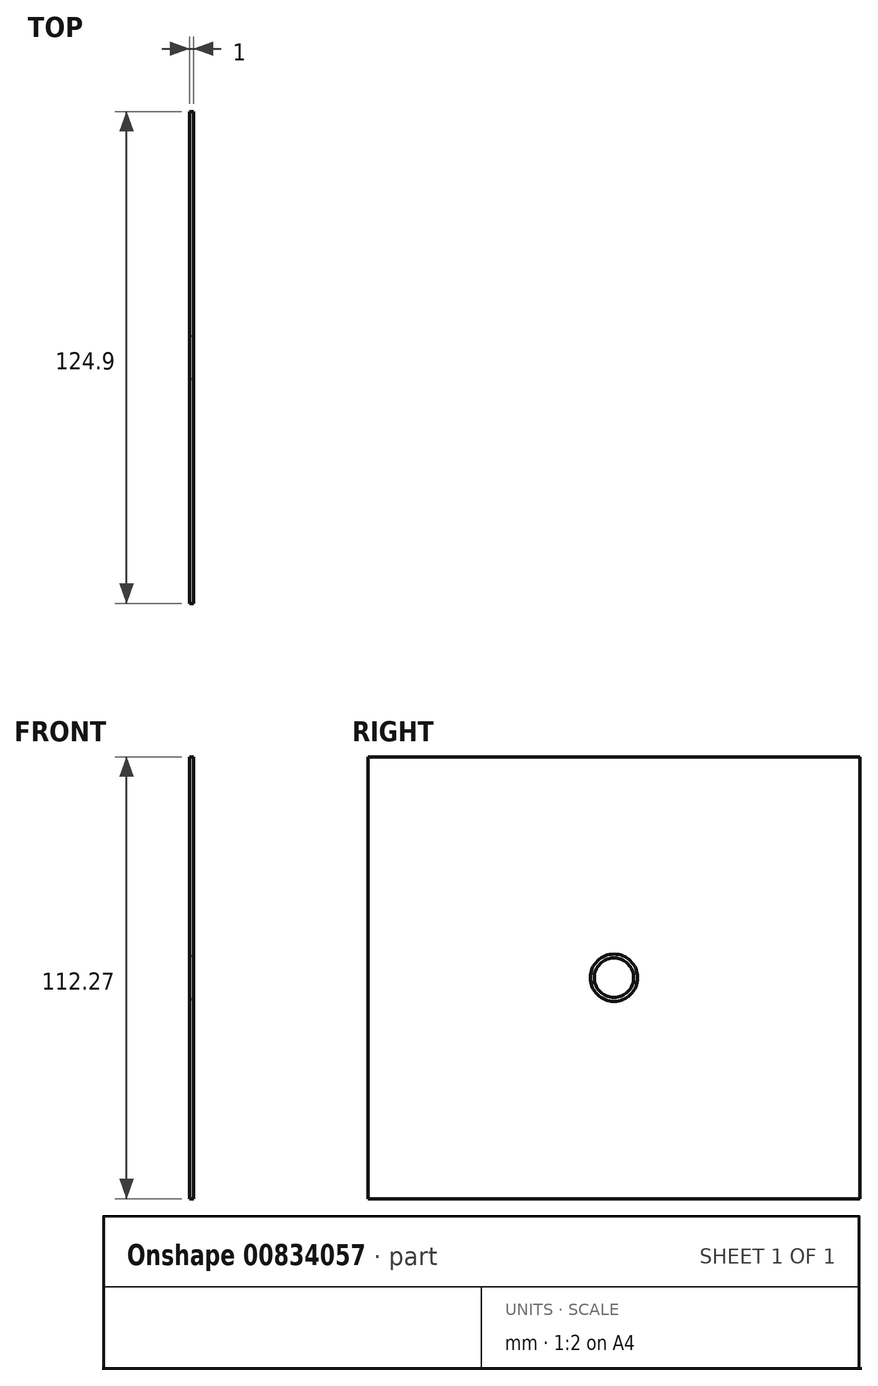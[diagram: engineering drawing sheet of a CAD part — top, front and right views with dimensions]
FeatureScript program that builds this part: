
annotation { "Feature Type Name" : "Feature", "Feature Type Description" : "" }
export const myFeature = defineFeature(function(context is Context, id is Id, definition is map)
    precondition{}
    {
        {
            var Q0;
            Q0=qCreatedBy(makeId("Right.planeOp"),FACE);
            var sketch = newSketch(context, id + "F0", { "sketchPlane" : qUnion([Q0])});
            skLineSegment(sketch, "E0.bottom", {"start": v(2.17, 0) * mm, "end": v(127.07, 0) * mm});
            skLineSegment(sketch, "E0.top", {"start": v(2.17, 112.27) * mm, "end": v(127.07, 112.27) * mm});
            skLineSegment(sketch, "E0.left", {"start": v(2.17, 0) * mm, "end": v(2.17, 112.27) * mm});
            skLineSegment(sketch, "E0.right", {"start": v(127.07, 0) * mm, "end": v(127.07, 112.27) * mm});
            skSolve(sketch);
        }
        {
            var Q0;
            Q0 = qSketchRegion(id + "F0", true);
            extrude(context, id + "F1", {"entities" : qUnion([Q0]), "depth" : 1 * mm, "offsetDistance" : 25 * mm});
        }
        {
            var Q0;
            Q0=makeQuery(id+"F1.opExtrude","CAP_FACE",FACE,{"disambiguationData":[OSD([sQuery(id+"F0.wireOp",EDGE,"E0.bottom"),sQuery(id+"F0.wireOp",EDGE,"E0.top"),sQuery(id+"F0.wireOp",EDGE,"E0.left"),sQuery(id+"F0.wireOp",EDGE,"E0.right")])],"isStart":false});
            var sketch = newSketch(context, id + "F2", { "sketchPlane" : qUnion([Q0])});
            skLineSegment(sketch, "E1", {"start": v(2.17, 56.13) * mm, "end": v(127.07, 56.13) * mm, "construction": true});
            skLineSegment(sketch, "E2", {"start": v(64.62, 112.27) * mm, "end": v(64.62, 0) * mm, "construction": true});
            skPoint(sketch, "E3", {"position": v(64.62, 56.13) * mm});
            skSolve(sketch);
        }
        {
            var Q0;
            Q0=sQuery(id+"F2.wireOp",VERTEX,"E3");
            var Q1;
            Q1=makeQuery(id+"F1.opExtrude","SWEPT_BODY",BODY,{"disambiguationData":[OSD([sQuery(id+"F0.wireOp",EDGE,"E0.bottom"),sQuery(id+"F0.wireOp",EDGE,"E0.top"),sQuery(id+"F0.wireOp",EDGE,"E0.left"),sQuery(id+"F0.wireOp",EDGE,"E0.right")])]});
            hole(context, id + "F3", {"style" : HoleStyle.C_SINK, "endStyle" : HoleEndStyle.THROUGH, "holeDiameter" : 6 * mm, "cSinkDiameter" : 12 * mm, "cSinkAngle" : 90 * degree, "majorDiameter" : 5 * mm, "isTappedThrough" : true, "tappedDepth" : 12 * mm, "tapClearance" : 3, "locations" : qUnion([Q0]), "scope" : qUnion([Q1])});
        }
    });
